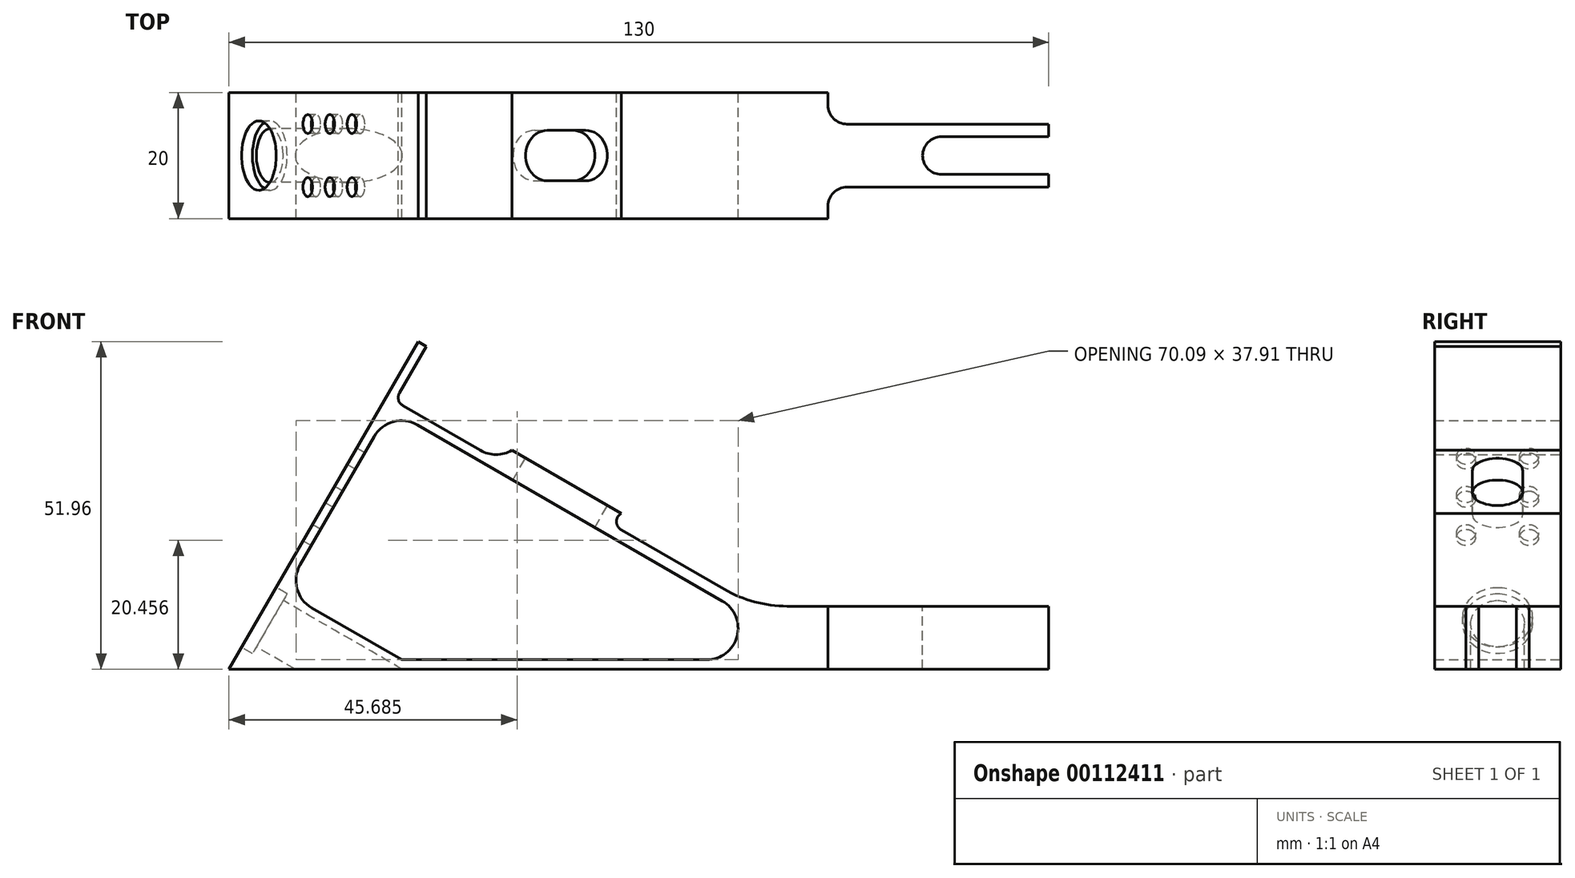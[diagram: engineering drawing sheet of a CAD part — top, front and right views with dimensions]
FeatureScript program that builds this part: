
annotation { "Feature Type Name" : "Feature", "Feature Type Description" : "" }
export const myFeature = defineFeature(function(context is Context, id is Id, definition is map)
    precondition{}
    {
        {
            var Q0;
            Q0=qCreatedBy(makeId("Front.planeOp"),FACE);
            var sketch = newSketch(context, id + "F0", { "sketchPlane" : qUnion([Q0])});
            skLineSegment(sketch, "E0", {"start": v(0, 0) * mm, "end": v(130, 0) * mm});
            skLineSegment(sketch, "E1", {"start": v(0, 0) * mm, "end": v(30, 51.96) * mm});
            skLineSegment(sketch, "E2", {"start": v(30, 51.96) * mm, "end": v(31.3, 51.21) * mm});
            skLineSegment(sketch, "E3", {"start": v(31.3, 51.21) * mm, "end": v(27.05, 43.85) * mm});
            skArc(sketch, "E4", {"start": v(27.05, 43.85) * mm, "mid": v(26.9, 42.71) * mm, "end": v(27.6, 41.8) * mm});
            skLineSegment(sketch, "E5", {"start": v(27.6, 41.8) * mm, "end": v(39.87, 34.72) * mm});
            skArc(sketch, "E6", {"start": v(39.87, 34.72) * mm, "mid": v(42.37, 34.05) * mm, "end": v(44.87, 34.72) * mm});
            skLineSegment(sketch, "E7", {"start": v(44.87, 34.72) * mm, "end": v(62.2, 24.72) * mm});
            skArc(sketch, "E8", {"start": v(62.2, 24.72) * mm, "mid": v(61.44, 23.42) * mm, "end": v(62.2, 22.12) * mm});
            skLineSegment(sketch, "E9", {"start": v(62.2, 22.12) * mm, "end": v(78.54, 12.68) * mm});
            skArc(sketch, "E10", {"start": v(78.54, 12.68) * mm, "mid": v(83.36, 10.68) * mm, "end": v(88.54, 10) * mm});
            skLineSegment(sketch, "E11", {"start": v(88.54, 10) * mm, "end": v(130, 10) * mm});
            skLineSegment(sketch, "E12", {"start": v(130, 10) * mm, "end": v(130, 0) * mm});
            skLineSegment(sketch, "E13", {"start": v(11.3, 16.57) * mm, "end": v(23.05, 36.92) * mm});
            skArc(sketch, "E14", {"start": v(23.05, 36.92) * mm, "mid": v(26.09, 39.25) * mm, "end": v(29.88, 38.75) * mm});
            skLineSegment(sketch, "E15", {"start": v(29.88, 38.75) * mm, "end": v(78.24, 10.83) * mm});
            skLineSegment(sketch, "E16", {"start": v(75.74, 1.5) * mm, "end": v(27.4, 1.5) * mm});
            skLineSegment(sketch, "E17", {"start": v(27.4, 1.5) * mm, "end": v(13.13, 9.74) * mm});
            skArc(sketch, "E18", {"start": v(11.3, 16.57) * mm, "mid": v(10.8, 12.78) * mm, "end": v(13.13, 9.74) * mm});
            skArc(sketch, "E19", {"start": v(75.74, 1.5) * mm, "mid": v(80.57, 5.2) * mm, "end": v(78.24, 10.83) * mm});
            skSolve(sketch);
        }
        {
            var Q0;
            Q0=makeQuery(id+"F0.imprint","IMPRINT",FACE,{"disambiguationData":[TD([[makeQuery(id+"F0.imprint","IMPRINT",EDGE,{"derivedFrom":sQuery(id+"F0.wireOp",EDGE,"E0")}),1.0]])]});
            extrude(context, id + "F1", {"entities" : qUnion([Q0]), "endBound" : BoundingType.SYMMETRIC, "depth" : 20 * mm});
        }
        {
            var Q0;
            Q0=makeQuery(id+"F1.opExtrude","SWEPT_FACE",FACE,{"disambiguationData":[OSD([sQuery(id+"F0.wireOp",EDGE,"E7")])]});
            var sketch = newSketch(context, id + "F2", { "sketchPlane" : qUnion([Q0])});
            skLineSegment(sketch, "E20", {"start": v(0, 0) * mm, "end": v(28, 0) * mm, "construction": true});
            skPoint(sketch, "E20.endSnap0", {"position": v(41.5, 0) * mm});
            skLineSegment(sketch, "E21", {"start": v(28, 0) * mm, "end": v(35, 0) * mm, "construction": true});
            skArc(sketch, "E22.0.startCap", {"start": v(28, -4) * mm, "mid": v(24, 0) * mm, "end": v(28, 4) * mm});
            skArc(sketch, "E22.0.endCap", {"start": v(35, 4) * mm, "mid": v(39, 0) * mm, "end": v(35, -4) * mm});
            skLineSegment(sketch, "E22.0.left", {"start": v(28, 4) * mm, "end": v(35, 4) * mm});
            skLineSegment(sketch, "E22.0.right", {"start": v(28, -4) * mm, "end": v(35, -4) * mm});
            skSolve(sketch);
        }
        {
            var Q0;
            Q0=makeQuery(id+"F1.opExtrude","SWEPT_FACE",FACE,{"disambiguationData":[OSD([sQuery(id+"F0.wireOp",EDGE,"E1")])]});
            cPlane(context, id + "F3", {"entities" : qUnion([Q0]), "cplaneType" : CPlaneType.OFFSET, "offset" : 25 * mm, "width" : 150 * mm, "height" : 150 * mm});
        }
        {
            var Q0;
            Q0 = qSketchRegion(id + "F2", true);
            extrude(context, id + "F4", {"entities" : qUnion([Q0]), "operationType" : NewBodyOperationType.REMOVE, "oppositeDirection" : true, "depth" : 8 * mm});
        }
        {
            var Q0;
            Q0=qCreatedBy(id+"F3.planeOp",FACE);
            var sketch = newSketch(context, id + "F5", { "sketchPlane" : qUnion([Q0])});
            skCircle(sketch, "E23", {"center": v(0, 9.5) * mm, "radius": 4.25 * mm});
            skCircle(sketch, "E24", {"center": v(0, 9.5) * mm, "radius": 5.5 * mm});
            skCircle(sketch, "E25", {"center": v(-5, 25) * mm, "radius": 1.5 * mm});
            skCircle(sketch, "E26", {"center": v(5, 25) * mm, "radius": 1.5 * mm});
            skCircle(sketch, "E27", {"center": v(-5, 32) * mm, "radius": 1.5 * mm});
            skCircle(sketch, "E28", {"center": v(5, 32) * mm, "radius": 1.5 * mm});
            skCircle(sketch, "E29", {"center": v(-5, 39) * mm, "radius": 1.5 * mm});
            skCircle(sketch, "E30", {"center": v(5, 39) * mm, "radius": 1.5 * mm});
            skLineSegment(sketch, "E31", {"start": v(0, 9.5) * mm, "end": v(0, 44.26) * mm, "construction": true});
            skSolve(sketch);
        }
        {
            var Q0;
            Q0=makeQuery(id+"F5.imprint","IMPRINT",FACE,{"disambiguationData":[TD([[makeQuery(id+"F5.imprint","IMPRINT",EDGE,{"derivedFrom":sQuery(id+"F5.wireOp",EDGE,"E29")}),1.0]])]});
            var Q1;
            Q1=makeQuery(id+"F5.imprint","IMPRINT",FACE,{"disambiguationData":[TD([[makeQuery(id+"F5.imprint","IMPRINT",EDGE,{"derivedFrom":sQuery(id+"F5.wireOp",EDGE,"E30")}),1.0]])]});
            var Q2;
            Q2=makeQuery(id+"F5.imprint","IMPRINT",FACE,{"disambiguationData":[TD([[makeQuery(id+"F5.imprint","IMPRINT",EDGE,{"derivedFrom":sQuery(id+"F5.wireOp",EDGE,"E27")}),1.0]])]});
            var Q3;
            Q3=makeQuery(id+"F5.imprint","IMPRINT",FACE,{"disambiguationData":[TD([[makeQuery(id+"F5.imprint","IMPRINT",EDGE,{"derivedFrom":sQuery(id+"F5.wireOp",EDGE,"E28")}),1.0]])]});
            var Q4;
            Q4=makeQuery(id+"F5.imprint","IMPRINT",FACE,{"disambiguationData":[TD([[makeQuery(id+"F5.imprint","IMPRINT",EDGE,{"derivedFrom":sQuery(id+"F5.wireOp",EDGE,"E26")}),1.0]])]});
            var Q5;
            Q5=makeQuery(id+"F5.imprint","IMPRINT",FACE,{"disambiguationData":[TD([[makeQuery(id+"F5.imprint","IMPRINT",EDGE,{"derivedFrom":sQuery(id+"F5.wireOp",EDGE,"E25")}),1.0]])]});
            extrude(context, id + "F6", {"entities" : qUnion([Q0, Q1, Q2, Q3, Q4, Q5]), "operationType" : NewBodyOperationType.REMOVE, "oppositeDirection" : true, "depth" : 30.83 * mm});
        }
        {
            var Q0;
            Q0=makeQuery(id+"F1.opExtrude","SWEPT_FACE",FACE,{"disambiguationData":[OSD([sQuery(id+"F0.wireOp",EDGE,"E1")])]});
            var sketch = newSketch(context, id + "F7", { "sketchPlane" : qUnion([Q0])});
            skCircle(sketch, "E32.0", {"center": v(0, 9.5) * mm, "radius": 5.5 * mm});
            skCircle(sketch, "E32.1", {"center": v(0, 9.5) * mm, "radius": 4.25 * mm});
            skSolve(sketch);
        }
        {
            var Q0;
            Q0 = qSketchRegion(id + "F7", true);
            extrude(context, id + "F8", {"entities" : qUnion([Q0]), "operationType" : NewBodyOperationType.REMOVE, "oppositeDirection" : true, "depth" : 2 * mm});
        }
        {
            var Q0;
            Q0=makeQuery(id+"F8.boolean.opBoolean","SPLIT",FACE,{"disambiguationData":[TD([makeQuery(id+"F8.opExtrude","SWEPT_FACE",FACE,{"disambiguationData":[OSD([sQuery(id+"F7.wireOp",EDGE,"E32.1")])]})])],"derivedFrom":makeQuery(id+"F1.opExtrude","SWEPT_FACE",FACE,{"disambiguationData":[OSD([sQuery(id+"F0.wireOp",EDGE,"E1")])]})});
            extrude(context, id + "F9", {"entities" : qUnion([Q0]), "operationType" : NewBodyOperationType.REMOVE, "endBound" : BoundingType.THROUGH_ALL, "oppositeDirection" : true, "depth" : 25 * mm});
        }
        {
            var Q0;
            Q0=makeQuery(id+"F1.opExtrude","SWEPT_FACE",FACE,{"disambiguationData":[OSD([sQuery(id+"F0.wireOp",EDGE,"E11")])]});
            var sketch = newSketch(context, id + "F10", { "sketchPlane" : qUnion([Q0])});
            skLineSegment(sketch, "E33", {"start": v(98, 5) * mm, "end": v(130, 5) * mm});
            skLineSegment(sketch, "E34", {"start": v(130, 5) * mm, "end": v(130, 3) * mm});
            skLineSegment(sketch, "E35", {"start": v(130, 3) * mm, "end": v(113, 3) * mm});
            skLineSegment(sketch, "E36", {"start": v(98, -5) * mm, "end": v(130, -5) * mm});
            skLineSegment(sketch, "E37", {"start": v(130, -5) * mm, "end": v(130, -3) * mm});
            skLineSegment(sketch, "E38", {"start": v(130, -3) * mm, "end": v(113, -3) * mm});
            skArc(sketch, "E39", {"start": v(113, 3) * mm, "mid": v(110, 0) * mm, "end": v(113, -3) * mm});
            skArc(sketch, "E40", {"start": v(98, 5) * mm, "mid": v(95.88, 5.88) * mm, "end": v(95, 8) * mm});
            skArc(sketch, "E41", {"start": v(98, -5) * mm, "mid": v(95.88, -5.88) * mm, "end": v(95, -8) * mm});
            skLineSegment(sketch, "E42", {"start": v(95, 8) * mm, "end": v(95, 10) * mm});
            skLineSegment(sketch, "E43", {"start": v(95, -8) * mm, "end": v(95, -10) * mm});
            skSolve(sketch);
        }
        {
            var Q0;
            {var subQ4=sQuery(id+"F10.wireOp",EDGE,"E33");Q0=makeQuery(id+"F10.imprint","IMPRINT",FACE,{"disambiguationData":[TD([[makeQuery(id+"F10.imprint","IMPRINT",EDGE,{"derivedFrom":subQ4}),1.0]])]});}
            var Q1;
            {var subQ0=sQuery(id+"F10.wireOp",EDGE,"E35");Q1=makeQuery(id+"F10.imprint","IMPRINT",FACE,{"disambiguationData":[TD([[makeQuery(id+"F10.imprint","IMPRINT",EDGE,{"derivedFrom":subQ0}),1.0]])]});}
            var Q2;
            {var subQ4=sQuery(id+"F10.wireOp",EDGE,"E36");Q2=makeQuery(id+"F10.imprint","IMPRINT",FACE,{"disambiguationData":[TD([[makeQuery(id+"F10.imprint","IMPRINT",EDGE,{"derivedFrom":subQ4}),-1.0]])]});}
            extrude(context, id + "F11", {"entities" : qUnion([Q0, Q1, Q2]), "operationType" : NewBodyOperationType.REMOVE, "oppositeDirection" : true, "depth" : 25 * mm});
        }
    });
